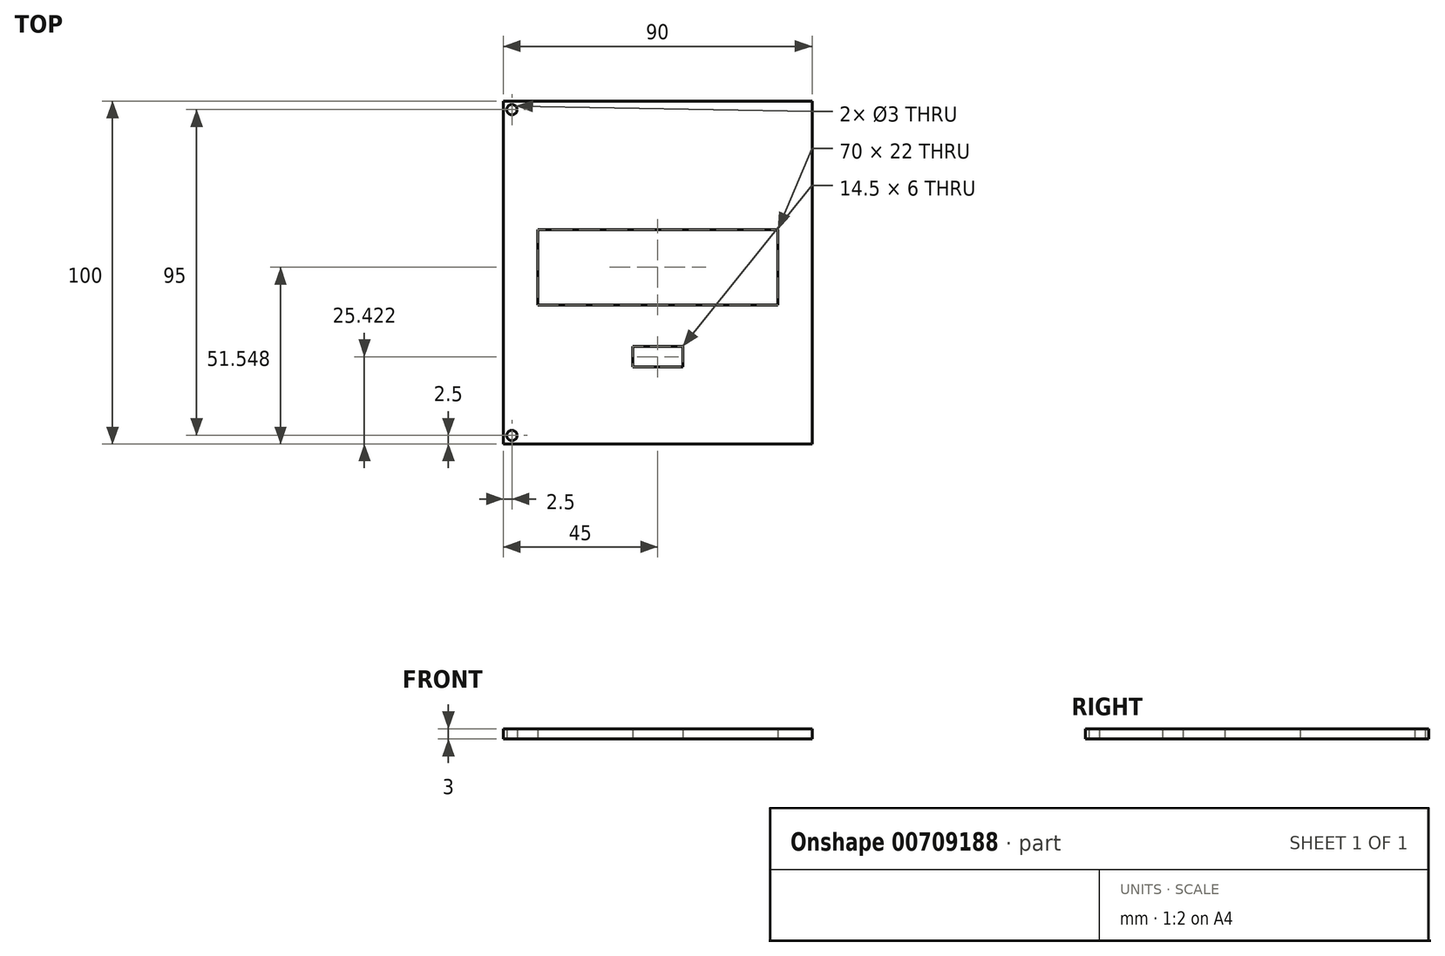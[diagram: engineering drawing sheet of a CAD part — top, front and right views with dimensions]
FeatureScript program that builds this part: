
annotation { "Feature Type Name" : "Feature", "Feature Type Description" : "" }
export const myFeature = defineFeature(function(context is Context, id is Id, definition is map)
    precondition{}
    {
        {
            var Q0;
            Q0=qCreatedBy(makeId("Top.planeOp"),FACE);
            var sketch = newSketch(context, id + "F0", { "sketchPlane" : qUnion([Q0])});
            skLineSegment(sketch, "E0.bottom", {"start": v(-60, 50) * mm, "end": v(30, 50) * mm});
            skLineSegment(sketch, "E0.top", {"start": v(-60, -50) * mm, "end": v(30, -50) * mm});
            skLineSegment(sketch, "E0.left", {"start": v(-60, 50) * mm, "end": v(-60, -50) * mm});
            skLineSegment(sketch, "E0.right", {"start": v(30, 50) * mm, "end": v(30, -50) * mm});
            skPoint(sketch, "E1", {"position": v(-57.5, 47.5) * mm});
            skPoint(sketch, "E2", {"position": v(57.5, 47.5) * mm});
            skPoint(sketch, "E3", {"position": v(57.5, -47.5) * mm});
            skPoint(sketch, "E4", {"position": v(-57.5, -47.5) * mm});
            skLineSegment(sketch, "E5", {"start": v(-15, 50) * mm, "end": v(-15, -50) * mm});
            skLineSegment(sketch, "E6.bottom", {"start": v(-50, 12.55) * mm, "end": v(20, 12.55) * mm});
            skLineSegment(sketch, "E6.top", {"start": v(-50, -9.45) * mm, "end": v(20, -9.45) * mm});
            skLineSegment(sketch, "E6.left", {"start": v(-50, 12.55) * mm, "end": v(-50, -9.45) * mm});
            skLineSegment(sketch, "E6.right", {"start": v(20, 12.55) * mm, "end": v(20, -9.45) * mm});
            skLineSegment(sketch, "E7.bottom", {"start": v(-22.25, -21.58) * mm, "end": v(-7.75, -21.58) * mm});
            skLineSegment(sketch, "E7.top", {"start": v(-22.25, -27.58) * mm, "end": v(-7.75, -27.58) * mm});
            skLineSegment(sketch, "E7.left", {"start": v(-22.25, -21.58) * mm, "end": v(-22.25, -27.58) * mm});
            skLineSegment(sketch, "E7.right", {"start": v(-7.75, -21.58) * mm, "end": v(-7.75, -27.58) * mm});
            skSolve(sketch);
        }
        {
            var Q0;
            {var subQ12=sQuery(id+"F0.wireOp",EDGE,"E0.left");Q0=makeQuery(id+"F0.imprint","IMPRINT",FACE,{"disambiguationData":[TD([[makeQuery(id+"F0.imprint","IMPRINT",EDGE,{"derivedFrom":subQ12}),1.0]])]});}
            var Q1;
            {var subQ13=sQuery(id+"F0.wireOp",EDGE,"E0.right");Q1=makeQuery(id+"F0.imprint","IMPRINT",FACE,{"disambiguationData":[TD([[makeQuery(id+"F0.imprint","IMPRINT",EDGE,{"derivedFrom":subQ13}),-1.0]])]});}
            extrude(context, id + "F1", {"entities" : qUnion([Q0, Q1]), "depth" : 3 * mm, "offsetDistance" : 25 * mm});
        }
        {
            var Q0;
            Q0=sQuery(id+"F0.wireOp",VERTEX,"E1");
            var Q1;
            Q1=sQuery(id+"F0.wireOp",VERTEX,"E2");
            var Q2;
            Q2=sQuery(id+"F0.wireOp",VERTEX,"E3");
            var Q3;
            Q3=sQuery(id+"F0.wireOp",VERTEX,"E4");
            var Q4;
            Q4=makeQuery(id+"F1.opExtrude","SWEPT_BODY",BODY,{"disambiguationData":[OSD([sQuery(id+"F0.wireOp",EDGE,"E0.bottom"),sQuery(id+"F0.wireOp",EDGE,"E0.top"),sQuery(id+"F0.wireOp",EDGE,"E0.left"),sQuery(id+"F0.wireOp",EDGE,"E0.right"),sQuery(id+"F0.wireOp",EDGE,"E6.bottom"),sQuery(id+"F0.wireOp",EDGE,"E6.top"),sQuery(id+"F0.wireOp",EDGE,"E6.left"),sQuery(id+"F0.wireOp",EDGE,"E6.right"),sQuery(id+"F0.wireOp",EDGE,"E7.bottom"),sQuery(id+"F0.wireOp",EDGE,"E7.top"),sQuery(id+"F0.wireOp",EDGE,"E7.left"),sQuery(id+"F0.wireOp",EDGE,"E7.right")])]});
            hole(context, id + "F2", {"style" : HoleStyle.SIMPLE, "endStyle" : HoleEndStyle.THROUGH, "oppositeDirection" : true, "holeDiameter" : 3 * mm, "majorDiameter" : 5 * mm, "isTappedThrough" : true, "tappedDepth" : 12 * mm, "tapClearance" : 3, "locations" : qUnion([Q0, Q1, Q2, Q3]), "scope" : qUnion([Q4])});
        }
    });
